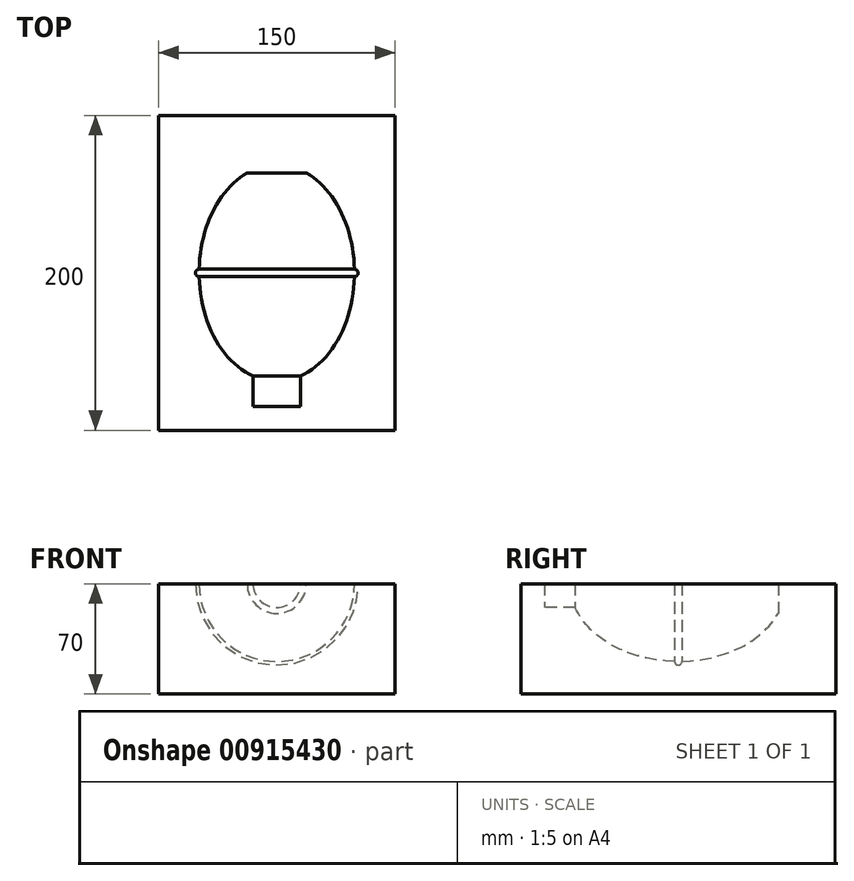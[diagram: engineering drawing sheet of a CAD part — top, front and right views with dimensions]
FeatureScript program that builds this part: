
annotation { "Feature Type Name" : "Feature", "Feature Type Description" : "" }
export const myFeature = defineFeature(function(context is Context, id is Id, definition is map)
    precondition{}
    {
        {
            var Q0;
            Q0=qCreatedBy(makeId("Top.planeOp"),FACE);
            var sketch = newSketch(context, id + "F0", { "sketchPlane" : qUnion([Q0])});
            skLineSegment(sketch, "E0.bottom", {"start": v(75, -100) * mm, "end": v(-75, -100) * mm});
            skLineSegment(sketch, "E0.top", {"start": v(75, 100) * mm, "end": v(-75, 100) * mm});
            skLineSegment(sketch, "E0.left", {"start": v(75, -100) * mm, "end": v(75, 100) * mm});
            skLineSegment(sketch, "E0.right", {"start": v(-75, -100) * mm, "end": v(-75, 100) * mm});
            skPoint(sketch, "E0.middle", {"position": v(0, 0) * mm});
            skSolve(sketch);
        }
        {
            var Q0;
            Q0=makeQuery(id+"F0.imprint","IMPRINT",FACE,{"disambiguationData":[TD([[makeQuery(id+"F0.imprint","IMPRINT",EDGE,{"derivedFrom":sQuery(id+"F0.wireOp",EDGE,"E0.bottom")}),-1.0]])]});
            extrude(context, id + "F1", {"entities" : qUnion([Q0]), "depth" : 50 * mm, "offsetDistance" : 25 * mm});
        }
        {
            var Q0;
            Q0=makeQuery(id+"F1.opExtrude","CAP_FACE",FACE,{"disambiguationData":[OSD([sQuery(id+"F0.wireOp",EDGE,"E0.bottom"),sQuery(id+"F0.wireOp",EDGE,"E0.top"),sQuery(id+"F0.wireOp",EDGE,"E0.left"),sQuery(id+"F0.wireOp",EDGE,"E0.right")])],"isStart":false});
            var sketch = newSketch(context, id + "F2", { "sketchPlane" : qUnion([Q0])});
            skEllipse(sketch, "E1", {"center": v(0, 0) * mm, "majorRadius": 68.7 * mm, "minorRadius": 49.35 * mm, "majorAxis": v(0, -1)});
            skLineSegment(sketch, "E2", {"start": v(0, 68.7) * mm, "end": v(0, -68.7) * mm});
            skSolve(sketch);
        }
        {
            var Q0;
            {var subQ0=sQuery(id+"F2.wireOp",EDGE,"E2");Q0=makeQuery(id+"F2.imprint","IMPRINT",FACE,{"disambiguationData":[TD([[makeQuery(id+"F2.imprint","IMPRINT",EDGE,{"derivedFrom":subQ0}),-1.0]])]});}
            var Q1;
            Q1=sQuery(id+"F2.wireOp",EDGE,"E2");
            revolve(context, id + "F3", {"operationType" : NewBodyOperationType.REMOVE, "surfaceOperationType" : NewSurfaceOperationType.NEW, "entities" : qUnion([Q0]), "axis" : qUnion([Q1]), "revolveType" : RevolveType.FULL, "oppositeDirection" : true});
        }
        {
            var Q0;
            Q0=makeQuery(id+"F1.opExtrude","CAP_FACE",FACE,{"disambiguationData":[OSD([sQuery(id+"F0.wireOp",EDGE,"E0.bottom"),sQuery(id+"F0.wireOp",EDGE,"E0.top"),sQuery(id+"F0.wireOp",EDGE,"E0.left"),sQuery(id+"F0.wireOp",EDGE,"E0.right")])],"isStart":false});
            var sketch = newSketch(context, id + "F4", { "sketchPlane" : qUnion([Q0])});
            skLineSegment(sketch, "E3.bottom", {"start": v(15, -52.57) * mm, "end": v(-15, -52.57) * mm});
            skLineSegment(sketch, "E3.top", {"start": v(15, -84.84) * mm, "end": v(-15, -84.84) * mm});
            skLineSegment(sketch, "E3.left", {"start": v(15, -52.57) * mm, "end": v(15, -84.84) * mm});
            skLineSegment(sketch, "E3.right", {"start": v(-15, -52.57) * mm, "end": v(-15, -84.84) * mm});
            skPoint(sketch, "E3.middle", {"position": v(0, -68.7) * mm});
            skLineSegment(sketch, "E4", {"start": v(0, -68.7) * mm, "end": v(0, -100) * mm});
            skSolve(sketch);
        }
        {
            var Q0;
            {var subQ0=sQuery(id+"F4.wireOp",EDGE,"E3.left");var subQ1=sQuery(id+"F4.wireOp",EDGE,"E3.top");var subQ2=makeQuery(id+"F4.imprint","INTERSECT",VERTEX,{"derivedFrom":[subQ1,subQ0]});Q0=makeQuery(id+"F4.imprint","IMPRINT",FACE,{"disambiguationData":[TD([[makeQuery(id+"F4.imprint","IMPRINT",EDGE,{"disambiguationData":[TD([[subQ2,-1.0]])],"derivedFrom":subQ1}),-1.0]])]});}
            var Q1;
            Q1=sQuery(id+"F4.wireOp",EDGE,"E4");
            revolve(context, id + "F5", {"operationType" : NewBodyOperationType.REMOVE, "surfaceOperationType" : NewSurfaceOperationType.NEW, "entities" : qUnion([Q0]), "axis" : qUnion([Q1]), "revolveType" : RevolveType.FULL, "oppositeDirection" : true});
        }
        {
            var Q0;
            Q0=makeQuery(id+"F1.opExtrude","SWEPT_FACE",FACE,{"disambiguationData":[OSD([sQuery(id+"F0.wireOp",EDGE,"E0.top")])]});
            var sketch = newSketch(context, id + "F6", { "sketchPlane" : qUnion([Q0])});
            skLineSegment(sketch, "E5.bottom", {"start": v(-75, 4.79) * mm, "end": v(75, 4.79) * mm});
            skLineSegment(sketch, "E5.top", {"start": v(-75, 50) * mm, "end": v(75, 50) * mm});
            skLineSegment(sketch, "E5.left", {"start": v(-75, 4.79) * mm, "end": v(-75, 50) * mm});
            skLineSegment(sketch, "E5.right", {"start": v(75, 4.79) * mm, "end": v(75, 50) * mm});
            skSolve(sketch);
        }
        {
            var Q0;
            Q0 = qSketchRegion(id + "F6", true);
            extrude(context, id + "F7", {"entities" : qUnion([Q0]), "operationType" : NewBodyOperationType.ADD, "oppositeDirection" : true, "depth" : 36.47 * mm, "offsetDistance" : 25 * mm});
        }
        {
            var Q0;
            Q0=makeQuery(id+"F7.boolean.opBoolean","MERGE",FACE,{"derivedFrom":[makeQuery(id+"F1.opExtrude","CAP_FACE",FACE,{"disambiguationData":[OSD([sQuery(id+"F0.wireOp",EDGE,"E0.bottom"),sQuery(id+"F0.wireOp",EDGE,"E0.top"),sQuery(id+"F0.wireOp",EDGE,"E0.left"),sQuery(id+"F0.wireOp",EDGE,"E0.right")])],"isStart":false}),makeQuery(id+"F7.opExtrude","SWEPT_FACE",FACE,{"disambiguationData":[OSD([sQuery(id+"F6.wireOp",EDGE,"E5.top")])]})]});
            var sketch = newSketch(context, id + "F8", { "sketchPlane" : qUnion([Q0])});
            skCircle(sketch, "E6", {"center": v(-49.35, 0) * mm, "radius": 2.31 * mm});
            skLineSegment(sketch, "E7", {"start": v(0, 61.14) * mm, "end": v(0, -61.84) * mm, "construction": true});
            skPoint(sketch, "E7.startSnap0", {"position": v(0, 63.53) * mm});
            skSolve(sketch);
        }
        {
            var Q0;
            Q0 = qSketchRegion(id + "F0", true);
            extrude(context, id + "F9", {"entities" : qUnion([Q0]), "operationType" : NewBodyOperationType.ADD, "oppositeDirection" : true, "depth" : 20 * mm, "offsetDistance" : 25 * mm});
        }
        {
            var Q0;
            {var subQ0=sQuery(id+"F8.wireOp",EDGE,"E6");var subQ1=makeQuery(id+"F3.boolean.opBoolean","INTERSECT",EDGE,{"disambiguationData":[OD(0.0)],"derivedFrom":[makeQuery(id+"F1.opExtrude","CAP_FACE",FACE,{"disambiguationData":[OSD([sQuery(id+"F0.wireOp",EDGE,"E0.bottom"),sQuery(id+"F0.wireOp",EDGE,"E0.top"),sQuery(id+"F0.wireOp",EDGE,"E0.left"),sQuery(id+"F0.wireOp",EDGE,"E0.right")])],"isStart":false}),makeQuery(id+"F3.opRevolve","SWEPT_FACE",FACE,{"disambiguationData":[OSD([sQuery(id+"F2.wireOp",EDGE,"E1")])]})]});var subQ2=makeQuery(id+"F8.imprint","INTERSECT",VERTEX,{"disambiguationData":[OD(0.0)],"derivedFrom":[subQ1,subQ0]});Q0=makeQuery(id+"F8.imprint","IMPRINT",FACE,{"disambiguationData":[TD([[makeQuery(id+"F8.imprint","IMPRINT",EDGE,{"disambiguationData":[TD([[subQ2,1.0]])],"derivedFrom":subQ0}),1.0]])]});}
            var Q1;
            Q1=sQuery(id+"F8.wireOp",EDGE,"E7");
            revolve(context, id + "F10", {"operationType" : NewBodyOperationType.REMOVE, "surfaceOperationType" : NewSurfaceOperationType.NEW, "entities" : qUnion([Q0]), "axis" : qUnion([Q1]), "revolveType" : RevolveType.FULL, "oppositeDirection" : true});
        }
    });
